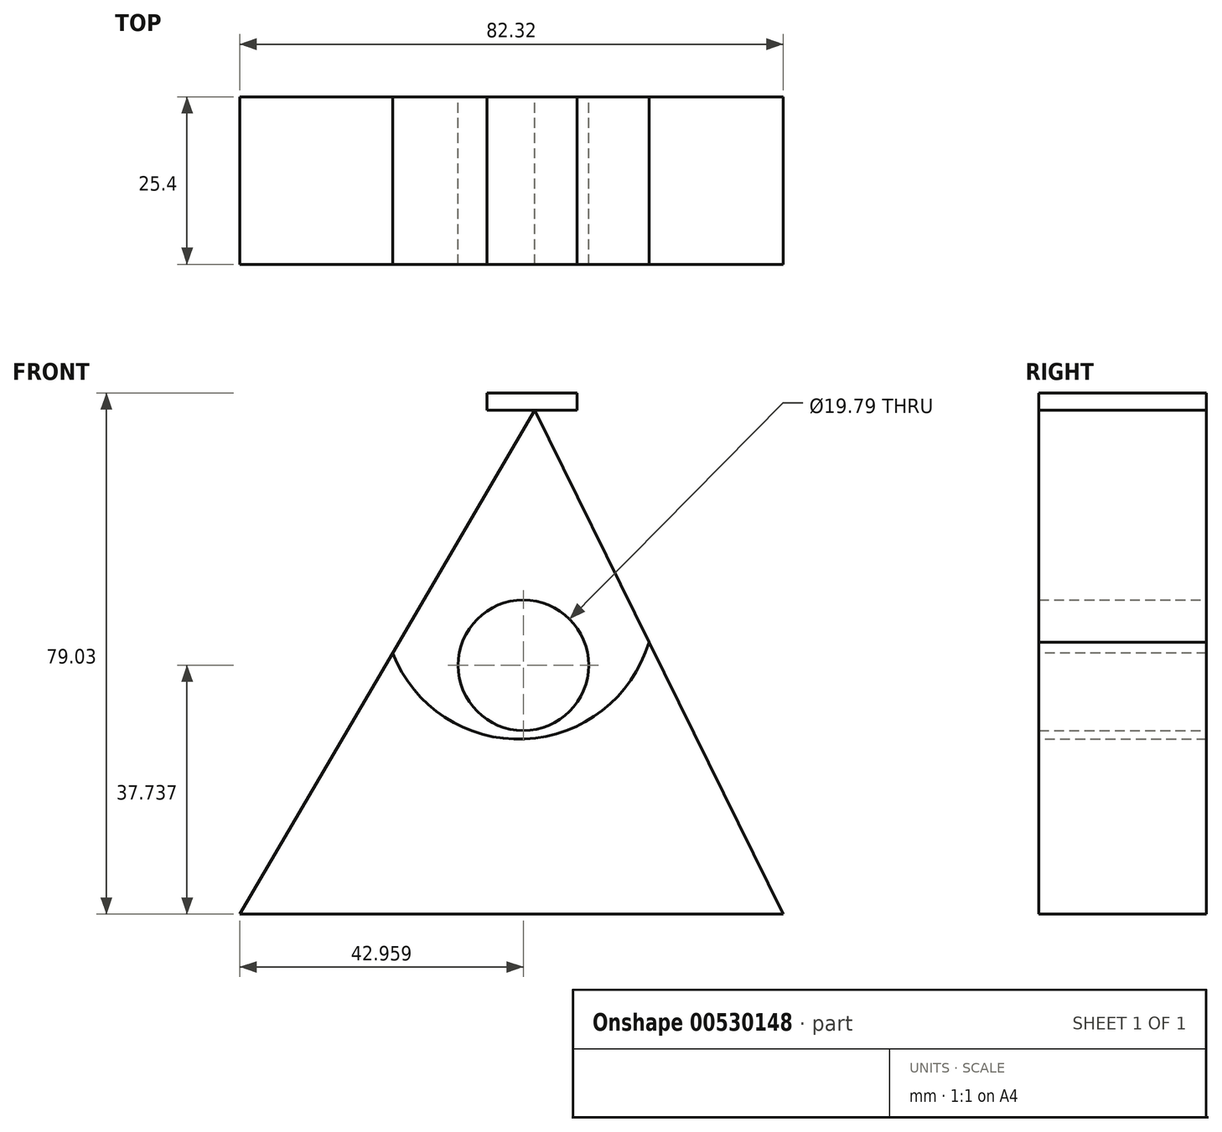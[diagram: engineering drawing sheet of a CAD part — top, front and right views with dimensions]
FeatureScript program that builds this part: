
annotation { "Feature Type Name" : "Feature", "Feature Type Description" : "" }
export const myFeature = defineFeature(function(context is Context, id is Id, definition is map)
    precondition{}
    {
        {
            var Q0;
            Q0=qCreatedBy(makeId("Front.planeOp"),FACE);
            var sketch = newSketch(context, id + "F0", { "sketchPlane" : qUnion([Q0])});
            skLineSegment(sketch, "E0", {"start": v(0, 76.42) * mm, "end": v(-44.67, 0) * mm});
            skLineSegment(sketch, "E1", {"start": v(-44.67, 0) * mm, "end": v(37.65, 0) * mm});
            skLineSegment(sketch, "E2", {"start": v(37.65, 0) * mm, "end": v(0, 76.42) * mm});
            skArc(sketch, "E3", {"start": v(17.32, 41.26) * mm, "mid": v(-2.4, 47.57) * mm, "end": v(-21.52, 39.6) * mm});
            skArc(sketch, "E4", {"start": v(-21.52, 39.6) * mm, "mid": v(-1.5, 26.55) * mm, "end": v(17.32, 41.26) * mm});
            skCircle(sketch, "E5", {"center": v(-1.71, 37.74) * mm, "radius": 9.9 * mm});
            skLineSegment(sketch, "E6.bottom", {"start": v(-7.24, 79.03) * mm, "end": v(6.45, 79.03) * mm});
            skLineSegment(sketch, "E6.top", {"start": v(-7.24, 76.42) * mm, "end": v(6.45, 76.42) * mm});
            skLineSegment(sketch, "E6.left", {"start": v(-7.24, 79.03) * mm, "end": v(-7.24, 76.42) * mm});
            skLineSegment(sketch, "E6.right", {"start": v(6.45, 79.03) * mm, "end": v(6.45, 76.42) * mm});
            skLineSegment(sketch, "E7.bottom", {"start": v(3.71, 79.03) * mm, "end": v(-3.99, 79.03) * mm});
            skLineSegment(sketch, "E7.top", {"start": v(3.71, 100.25) * mm, "end": v(-3.99, 100.25) * mm});
            skLineSegment(sketch, "E7.left", {"start": v(3.71, 79.03) * mm, "end": v(3.71, 100.25) * mm});
            skLineSegment(sketch, "E7.right", {"start": v(-3.99, 79.03) * mm, "end": v(-3.99, 100.25) * mm});
            skFitSpline(sketch, "E8", {"points": [v(-30.34, 0) * mm, v(-31.03, -15.44) * mm, v(-21.61, -10.65) * mm, v(-19.9, -15.96) * mm], "startDerivative": vector(-12, -55.6) * mm, "endDerivative": vector(0.76, -32.07) * mm});
            skFitSpline(sketch, "E9", {"points": [v(10.73, 0) * mm, v(8.68, -15.1) * mm, v(16.72, -10.65) * mm, v(19.29, -16.47) * mm], "startDerivative": vector(-15.24, -54.6) * mm, "endDerivative": vector(4.3, -33.1) * mm});
            skFitSpline(sketch, "E10", {"points": [v(-23.8, 35.7) * mm, v(-47.97, 23.58) * mm, v(-54.3, 38.8) * mm], "startDerivative": vector(-51.08, -37.41) * mm, "endDerivative": vector(-8.17, 47.09) * mm});
            skFitSpline(sketch, "E11", {"points": [v(19.87, 36.1) * mm, v(39.83, 24.43) * mm, v(53.52, 40.52) * mm], "startDerivative": vector(41.86, -37.06) * mm, "endDerivative": vector(25.32, 46.54) * mm});
            skFitSpline(sketch, "E12", {"points": [v(63.79, 15.7) * mm, v(53.52, 40.52) * mm, v(56.77, 45.83) * mm, v(61.22, 40.52) * mm], "startDerivative": vector(-31.98, 55.35) * mm, "endDerivative": vector(17.03, -31) * mm});
            skSolve(sketch);
        }
        {
            var Q0;
            {var subQ3=sQuery(id+"F0.wireOp",EDGE,"E6.left");Q0=makeQuery(id+"F0.imprint","IMPRINT",FACE,{"disambiguationData":[TD([[makeQuery(id+"F0.imprint","IMPRINT",EDGE,{"derivedFrom":subQ3}),1.0]])]});}
            var Q1;
            Q1=makeQuery(id+"F0.imprint","IMPRINT",FACE,{"disambiguationData":[TD([[makeQuery(id+"F0.imprint","IMPRINT",EDGE,{"derivedFrom":sQuery(id+"F0.wireOp",EDGE,"E7.bottom")}),-1.0]])]});
            var Q2;
            {var subQ1=sQuery(id+"F0.wireOp",EDGE,"E3");var subQ4=sQuery(id+"F0.wireOp",EDGE,"E5");var subQ9=makeQuery(id+"F0.imprint","INTERSECT",VERTEX,{"disambiguationData":[OD(0.0)],"derivedFrom":[subQ1,subQ4]});Q2=makeQuery(id+"F0.imprint","IMPRINT",FACE,{"disambiguationData":[TD([[makeQuery(id+"F0.imprint","IMPRINT",EDGE,{"disambiguationData":[TD([[subQ9,-1.0]])],"derivedFrom":subQ4}),-1.0]])]});}
            var Q3;
            {var subQ0=sQuery(id+"F0.wireOp",EDGE,"E4");Q3=makeQuery(id+"F0.imprint","IMPRINT",FACE,{"disambiguationData":[TD([[makeQuery(id+"F0.imprint","IMPRINT",EDGE,{"derivedFrom":subQ0}),1.0]])]});}
            extrude(context, id + "F1", {"entities" : qUnion([Q0, Q1, Q2, Q3]), "endBound" : BoundingType.SYMMETRIC, "depth" : 25.4 * mm, "offsetDistance" : 25.4 * mm});
        }
        {
            var Q0;
            {var subQ6=sQuery(id+"F0.wireOp",EDGE,"E4");Q0=makeQuery(id+"F0.imprint","IMPRINT",FACE,{"disambiguationData":[TD([[makeQuery(id+"F0.imprint","IMPRINT",EDGE,{"derivedFrom":subQ6}),-1.0]])]});}
            extrude(context, id + "F2", {"entities" : qUnion([Q0]), "endBound" : BoundingType.SYMMETRIC, "oppositeDirection" : true, "depth" : 25.4 * mm, "offsetDistance" : 25.4 * mm});
        }
    });
